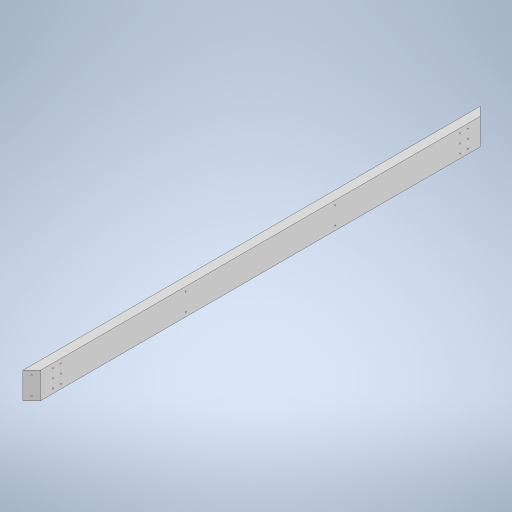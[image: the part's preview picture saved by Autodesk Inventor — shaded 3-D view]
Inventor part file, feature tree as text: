
AUTODESK INVENTOR PART (.ipt)
format: ipt  version: 2023 (Build 270158000, 158)  size: 434,176 bytes
history: native  units: in
note: dims shown in document units (in); Inventor stores cm internally (conversion verified against a paired STEP export)
features: other x9, hole x8, sketch x6, extrude x5, chamfer x2
ambient origin geometry x8: Origin, YZ Plane, XZ Plane, XY Plane, X Axis, Y Axis, Z Axis, Center Point
bodies: Solid1 (feature_tree)
feature tree (30):
  extrude  "Extrusion1"  Depth=54.0in
  sketch  "Sketch2"  dims[d2=1.0in d3=1.0in]
  extrude  "Extrusion2"  Depth=1.0in
  extrude  "Extrusion3"  Depth=16.0in
  other  "Work Axis1"
  other  "Work Axis2"
  other  "Work Axis3"
  other  "Work Point1"
  other  "Work Point2"
  other  "Work Axis4"
  other  "Work Axis5"
  other  "Work Point3"
  other  "Work Point4"
  hole  "Hole1"  [1 undecoded]
  hole  "Hole2"  [1 undecoded]
  hole  "Hole3"  [1 undecoded]
  hole  "Hole4"  [1 undecoded]
  hole  "Hole5"  [1 undecoded]
  hole  "Hole6"  [1 undecoded]
  hole  "Hole7"  [1 undecoded]
  hole  "Hole8"  [1 undecoded]
  extrude  "Extrusion4"  Depth=0.125in
  chamfer  "Chamfer1"  Distance=17.0in
  extrude  "Extrusion5"  Depth=0.125in
  chamfer  "Chamfer2"  Distance=20.0in
  sketch  "Sketch1"  dims[d0=54.0in d1=54.0in]
  sketch  "Sketch3"  dims[d4=8.0in d5=16.0in]
  sketch  "Sketch4"  dims[d6=8.0in d7=16.0in]
  sketch  "Sketch5"  dims[d8=16.0in d9=8.0in]
  sketch  "Sketch6"  dims[d10=16.0in d11=8.0in d12=4.0in d13=4.0in d14=4.0in d15=4.0in d16=17.0in d17=17.0in d18=17.0in d19=17.0in d20=20.0in d21=1.0in d22=1.0in d23=1.0in d24=1.0in d25=45.0deg d26=2.5in d27=45.0deg d28=45.0deg d29=45.0deg d30=1.0in d31=1.0in d32=1.0in d33=1.0in d34=0.25in d35=0.25in d36=0.25in d37=0.25in d38=0.25in d39=0.25in d40=0.25in d41=0.25in d42=3.0in d43=0.0in d44=0.125in d45=0.125in d46=0.707in d47=0.707in d48=0.5in d49=0.5in d50=3.0in d51=0.0in d52=0.125in d53=0.125in d54=0.707in d55=0.707in d56=0.5in d57=0.5in d58=3.0in d59=0.0in d60=1.0in d61=1.0in d62=0.25in d63=0.75in d64=0.375in d65=0.25in d66=0.5635in d67=0.15in d68=0.0in d69=1.0in d70=1.0in d71=0.25in d72=0.75in d73=0.375in d74=0.25in d75=0.5635in d76=0.15in d77=0.0in d78=1.0in d79=1.0in d80=0.25in d81=0.75in d82=0.375in d83=0.25in d84=0.5635in d85=0.15in d86=0.0in d87=1.0in d88=1.0in d89=0.25in d90=0.75in d91=0.375in d92=0.25in d93=0.5635in d94=0.15in d95=0.0in d96=1.0in d97=1.0in d98=0.25in d99=0.75in d100=0.375in d101=0.25in d102=0.5635in d103=0.15in d104=0.0in d105=1.0in d106=1.0in d107=0.25in d108=0.75in d109=0.375in d110=0.25in d111=0.5635in d112=0.15in d113=0.0in d114=1.0in d115=1.0in d116=0.25in d117=0.75in d118=0.375in d119=0.25in d120=0.5635in d121=0.15in d122=0.0in d123=1.0in d124=1.0in d125=0.25in d126=0.75in d127=0.375in d128=0.25in d129=0.5635in d130=0.15in d131=0.0in d132=0.125in d133=0.125in d134=0.5in d135=0.5in d136=0.5in d137=0.5in d138=0.125in d139=0.125in d140=0.5in d141=0.5in d142=0.5in d143=0.5in d144=3.0in d145=0.0in d146=0.125in d147=0.125in d148=45.0deg d149=0.125in d150=0.125in d151=0.125in d152=0.125in d153=0.125in d154=0.125in d155=0.5in d156=0.5in d157=1.5in d158=1.5in d159=0.5in d160=0.5in d161=1.414in d162=1.414in d163=1.414in d164=0.914in d165=0.914in d166=0.914in d167=3.0in d168=0.0in d169=0.125in d170=0.125in d171=45.0deg d172=26.0in]
note: 8 required parameter values undecoded (feature->parameter linkage not recoverable at this tier; creation-order binding heuristic only, values carry confidence <= 0.55)
